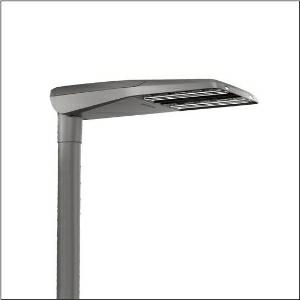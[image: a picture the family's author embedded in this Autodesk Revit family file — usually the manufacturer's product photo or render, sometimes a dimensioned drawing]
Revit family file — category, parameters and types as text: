
# Revit family: streetlight_sl_11_iq_midi___st1_2a_5xc3a41f08me_055e
name_source: partatom
category: Lighting Fixtures
units: mm (PartAtom-declared; Revit-internal decimal feet)

## family parameters
Cut with Voids When Loaded = No
Host = Face
Light Source = No
Part Type = Normal
Room Calculation Point = No
Round Connector Dimension = Use Diameter
Shared = No

## types (1)
- --- (1 x LED, 18900 lm, 124.7 W, 4000K)
    Apparent Load = 125 VA
    CIE Flux Codes = 32 70 96 100 100
    Color Rendering = 70
    Color Temperature = 4000K
    Default Elevation = 1800 mm
    Description = Streetlight SL 11 iQ midi, mast luminaire, primary light control with 3 zone facetted reflector, of plastic, silver coated, highly specular, primary optical cover: cover, of PMMA, transparent, light distribution: ST1.2a, light emission: direct distribution, primary light characteristic: asymmetric, installation type: post-top, side-entry, lamps: LED, High Power LED, rated values: 18.900lm | 124,7W | 151,6lm/W (begin service life); end service life: 18.900lm | 132,2W; at 50% lumin. flux: 9.450lm | 57,4W | 164,6lm/W, colour temperature: 4000K, colour rendering: CRI > 70, light colour: 740, light setting 1 begin service life: 100% | 18.900lm | 124,7W | 151,6lm/W | 4.000K, light setting 1 end service life: 132,2W, further light settings possible, control: Street-Remote, optimised constant luminous flux control (CLO 2.0), Desk-Remote (wireless, voltage-free reading and setting of iQ features in the workshop via application-optimized NFC function/RFID function), Light-Fading, Smart-Wire, Night-Set, Lumen-Switch, Temp-Guard, Auto-Match, with cable H07RN-F 3x 1.5mm², mains connection: 230..240V, AC, 50/60Hz, connection cable pre-assembled, cable length: 12,5m, luminaire housing, of diecast aluminium, powder-coated, SITECO metallic grey (DB 702S), please order mast flange separately, inclination adjustable without tools: 0°, 5°, 10°, 15° (post-top) | 0°, -5°, -10°, -15° (side-entry), sealing non-destructively replaceable, multi-level sealing system, length: 780mm, width: 376mm, height: 118mm, mast flange for spigot size: 42mm (side-entry): 5XC10008XM4, 60/48mm (side-entry/post-top): 5XC10108XM2, 76/60mm (side-entry/post-top): 5XC10108XM1, equipment: Power, protection rating (complete): IP66, insulation class (complete): insulation class II (safety insulation), certification: CE, ENEC, ENEC+, VDE, impact resistance: IK10, permissible operating ambient temperature for outdoor applications: -25..+50°C, standard-compliant lighting for roads and squares, Environmental Product Declaration (EPD) tested and certified by an independent institute, packaging unit: 1 piece

Light Distribution: ST1.2a
    Height = 118 mm
    Lamp = 1 x LED
    Lamp Light Flux = 18900 lm
    Lamp Power = 124.7 W
    Lamp count = 1
    Length = 780 mm
    Luminous efficacy = 152 lm/W
    Manufacturer = Siteco
    ModVariant = No
    Model = 5XC3A41F08ME
    Number of Poles = 1
    OnlyDefault = Yes
    Power Factor = 1
    Product Name = Streetlight SL 11 iQ midi | ST1.2a
    Product group = mast luminaire | pylon top
    ProductGroupID = 6100
    Protection Class = Protection class II
    Protection Degree = IP 66
    RLX_Detail_Level = 1
    RLX_Emergency_Light_Flux = 0 lm
    RLX_Emergency_Type = 0
    RLX_Emergency_Type_DB = No
    RlxData = <blob elided: 71073 chars, md5=7fba2f67>
    Socket = socket
    Standby Power = 0 W
    System Light Flux = 18900 lm
    System Power = 125 W
    Type Comments = factory setting: luminous flux: 100 % | dim-lin: 254 | 557 mA
    Type Image = l_1005960.jpg
    URL = http://relux.com
    VarID = @adj_193763
    Voltage = 0 V
    Weight = 0.00 kg
    Width = 376 mm

## geometry (parser evidence)
native form markers: Blend x4, Sweep x10
no freeform markers — native parametric forms only
